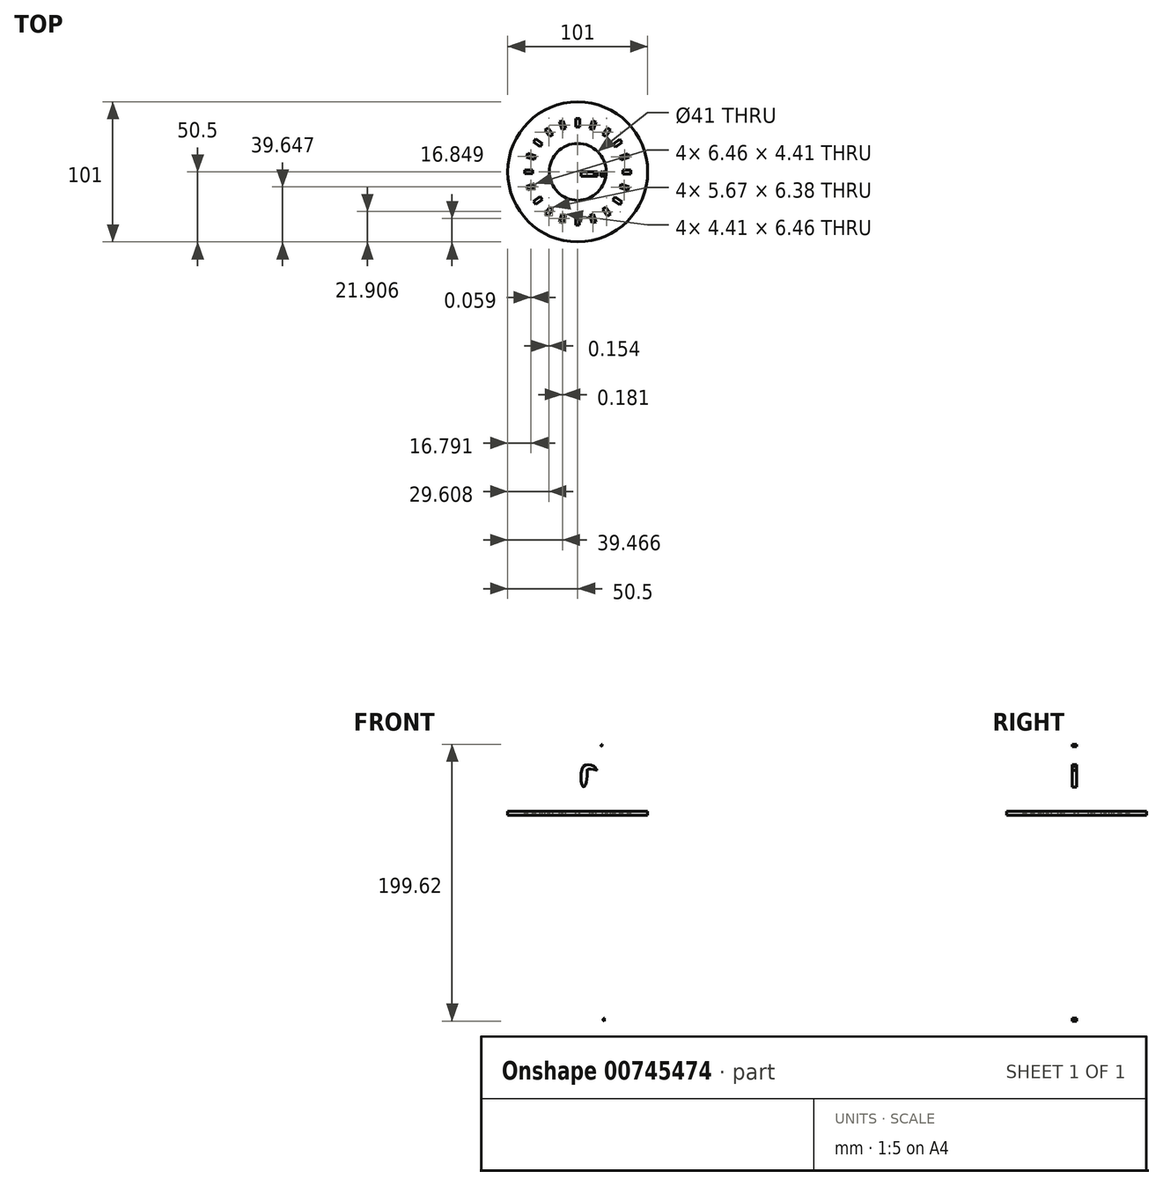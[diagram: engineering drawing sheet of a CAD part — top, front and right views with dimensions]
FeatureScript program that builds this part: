
annotation { "Feature Type Name" : "Feature", "Feature Type Description" : "" }
export const myFeature = defineFeature(function(context is Context, id is Id, definition is map)
    precondition{}
    {
        {
            var Q0;
            Q0=qCreatedBy(makeId("Front.planeOp"),FACE);
            var sketch = newSketch(context, id + "F0", { "sketchPlane" : qUnion([Q0])});
            skFitSpline(sketch, "E0", {"points": [v(18.94, 55.8) * mm, v(19.4, 42.74) * mm, v(74.56, -23) * mm, v(58.26, -54.69) * mm, v(18.93, -151.45) * mm], "startDerivative": vector(-29.4, -78.93) * mm, "endDerivative": vector(0, -157.02) * mm});
            skFitSpline(sketch, "E1.0", {"points": [v(9.57, 59.29) * mm, v(9.44, 58.92) * mm, v(9.1, 58.03) * mm, v(8.45, 56.18) * mm, v(7.84, 53.83) * mm, v(7.44, 51.02) * mm, v(7.45, 47.87) * mm, v(7.89, 45.1) * mm, v(8.5, 42.89) * mm, v(9.08, 41.22) * mm, v(9.67, 39.84) * mm, v(10.2, 38.74) * mm, v(10.64, 37.9) * mm, v(11.1, 37.1) * mm, v(11.72, 36.02) * mm, v(12.56, 34.7) * mm, v(13.65, 33.11) * mm, v(15.19, 31) * mm, v(17.29, 28.36) * mm, v(20.06, 25.1) * mm, v(23.05, 21.77) * mm, v(27.29, 17.22) * mm, v(32.95, 11.36) * mm, v(39.98, 4.2) * mm, v(46.9, -2.94) * mm, v(53.3, -9.85) * mm, v(57.89, -15.23) * mm, v(60.89, -19.14) * mm, v(62.74, -21.82) * mm, v(63.91, -23.77) * mm, v(64.6, -25.1) * mm, v(64.93, -25.82) * mm, v(65.13, -26.31) * mm, v(65.28, -26.74) * mm, v(65.42, -27.2) * mm, v(65.51, -27.62) * mm, v(65.56, -28.04) * mm, v(65.56, -28.36) * mm, v(65.5, -28.75) * mm, v(65.26, -29.42) * mm, v(64.73, -30.46) * mm, v(63.8, -31.88) * mm, v(62.48, -33.62) * mm, v(60.8, -35.67) * mm, v(58.8, -38.02) * mm, v(56.54, -40.67) * mm, v(54.08, -43.65) * mm, v(51.92, -46.42) * mm, v(50.14, -48.83) * mm, v(48.36, -51.35) * mm, v(46.15, -54.66) * mm, v(43.52, -58.88) * mm, v(40.9, -63.31) * mm, v(37.47, -69.48) * mm, v(33.27, -77.6) * mm, v(28.46, -87.76) * mm, v(23.96, -98.1) * mm, v(19.86, -108.39) * mm, v(16.26, -118.37) * mm, v(13.25, -127.84) * mm, v(11.3, -135.12) * mm, v(10.14, -140.51) * mm, v(9.48, -144.34) * mm, v(9.04, -147.97) * mm, v(8.93, -150.3) * mm, v(8.93, -151.45) * mm]});
            skLineSegment(sketch, "E2", {"start": v(18.94, 55.8) * mm, "end": v(8.37, 55.8) * mm});
            skLineSegment(sketch, "E3", {"start": v(18.93, -151.45) * mm, "end": v(8.93, -151.45) * mm});
            skLineSegment(sketch, "E4", {"start": v(14.05, 32.57) * mm, "end": v(16.18, 32.57) * mm});
            skFitSpline(sketch, "E5.trimOffspring", {"points": [v(9.57, 59.29) * mm, v(9.44, 58.92) * mm, v(9.1, 58.03) * mm, v(8.45, 56.18) * mm, v(7.84, 53.83) * mm, v(7.44, 51.02) * mm, v(7.45, 47.87) * mm, v(7.89, 45.1) * mm, v(8.5, 42.89) * mm, v(9.08, 41.22) * mm, v(9.67, 39.84) * mm, v(10.2, 38.74) * mm, v(10.64, 37.9) * mm, v(11.1, 37.1) * mm, v(11.72, 36.02) * mm, v(12.56, 34.7) * mm, v(13.65, 33.11) * mm, v(15.19, 31) * mm, v(17.29, 28.36) * mm, v(20.06, 25.1) * mm, v(23.05, 21.77) * mm, v(27.29, 17.22) * mm, v(32.95, 11.36) * mm, v(39.98, 4.2) * mm, v(46.9, -2.94) * mm, v(53.3, -9.85) * mm, v(57.89, -15.23) * mm, v(60.89, -19.14) * mm, v(62.74, -21.82) * mm, v(63.91, -23.77) * mm, v(64.6, -25.1) * mm, v(64.93, -25.82) * mm, v(65.13, -26.31) * mm, v(65.28, -26.74) * mm, v(65.42, -27.2) * mm, v(65.51, -27.62) * mm, v(65.56, -28.04) * mm, v(65.56, -28.36) * mm, v(65.5, -28.75) * mm, v(65.26, -29.42) * mm, v(64.73, -30.46) * mm, v(63.8, -31.88) * mm, v(62.48, -33.62) * mm, v(60.8, -35.67) * mm, v(58.8, -38.02) * mm, v(56.54, -40.67) * mm, v(54.08, -43.65) * mm, v(51.92, -46.42) * mm, v(50.14, -48.83) * mm, v(48.36, -51.35) * mm, v(46.15, -54.66) * mm, v(43.52, -58.88) * mm, v(40.9, -63.31) * mm, v(37.47, -69.48) * mm, v(33.27, -77.6) * mm, v(28.46, -87.76) * mm, v(23.96, -98.1) * mm, v(19.86, -108.39) * mm, v(16.26, -118.37) * mm, v(13.25, -127.84) * mm, v(11.3, -135.12) * mm, v(10.14, -140.51) * mm, v(9.48, -144.34) * mm, v(9.04, -147.97) * mm, v(8.93, -150.3) * mm, v(8.93, -151.45) * mm]});
            skFitSpline(sketch, "E6.trimOffspring", {"points": [v(9.57, 59.29) * mm, v(9.44, 58.92) * mm, v(9.1, 58.03) * mm, v(8.45, 56.18) * mm, v(7.84, 53.83) * mm, v(7.44, 51.02) * mm, v(7.45, 47.87) * mm, v(7.89, 45.1) * mm, v(8.5, 42.89) * mm, v(9.08, 41.22) * mm, v(9.67, 39.84) * mm, v(10.2, 38.74) * mm, v(10.64, 37.9) * mm, v(11.1, 37.1) * mm, v(11.72, 36.02) * mm, v(12.56, 34.7) * mm, v(13.65, 33.11) * mm, v(15.19, 31) * mm, v(17.29, 28.36) * mm, v(20.06, 25.1) * mm, v(23.05, 21.77) * mm, v(27.29, 17.22) * mm, v(32.95, 11.36) * mm, v(39.98, 4.2) * mm, v(46.9, -2.94) * mm, v(53.3, -9.85) * mm, v(57.89, -15.23) * mm, v(60.89, -19.14) * mm, v(62.74, -21.82) * mm, v(63.91, -23.77) * mm, v(64.6, -25.1) * mm, v(64.93, -25.82) * mm, v(65.13, -26.31) * mm, v(65.28, -26.74) * mm, v(65.42, -27.2) * mm, v(65.51, -27.62) * mm, v(65.56, -28.04) * mm, v(65.56, -28.36) * mm, v(65.5, -28.75) * mm, v(65.26, -29.42) * mm, v(64.73, -30.46) * mm, v(63.8, -31.88) * mm, v(62.48, -33.62) * mm, v(60.8, -35.67) * mm, v(58.8, -38.02) * mm, v(56.54, -40.67) * mm, v(54.08, -43.65) * mm, v(51.92, -46.42) * mm, v(50.14, -48.83) * mm, v(48.36, -51.35) * mm, v(46.15, -54.66) * mm, v(43.52, -58.88) * mm, v(40.9, -63.31) * mm, v(37.47, -69.48) * mm, v(33.27, -77.6) * mm, v(28.46, -87.76) * mm, v(23.96, -98.1) * mm, v(19.86, -108.39) * mm, v(16.26, -118.37) * mm, v(13.25, -127.84) * mm, v(11.3, -135.12) * mm, v(10.14, -140.51) * mm, v(9.48, -144.34) * mm, v(9.04, -147.97) * mm, v(8.93, -150.3) * mm, v(8.93, -151.45) * mm]});
            skLineSegment(sketch, "E7", {"start": v(42.73, 1.36) * mm, "end": v(42.73, 1.36) * mm});
            skPoint(sketch, "E8.orphan", {"position": v(0, -86.14) * mm});
            skPoint(sketch, "E9.end.orphan", {"position": v(15.52, -133.04) * mm});
            skFitSpline(sketch, "E10.trimOffspring", {"points": [v(9.57, 59.29) * mm, v(9.44, 58.92) * mm, v(9.1, 58.03) * mm, v(8.45, 56.18) * mm, v(7.84, 53.83) * mm, v(7.44, 51.02) * mm, v(7.45, 47.87) * mm, v(7.89, 45.1) * mm, v(8.5, 42.89) * mm, v(9.08, 41.22) * mm, v(9.67, 39.84) * mm, v(10.2, 38.74) * mm, v(10.64, 37.9) * mm, v(11.1, 37.1) * mm, v(11.72, 36.02) * mm, v(12.56, 34.7) * mm, v(13.65, 33.11) * mm, v(15.19, 31) * mm, v(17.29, 28.36) * mm, v(20.06, 25.1) * mm, v(23.05, 21.77) * mm, v(27.29, 17.22) * mm, v(32.95, 11.36) * mm, v(39.98, 4.2) * mm, v(46.9, -2.94) * mm, v(53.3, -9.85) * mm, v(57.89, -15.23) * mm, v(60.89, -19.14) * mm, v(62.74, -21.82) * mm, v(63.91, -23.77) * mm, v(64.6, -25.1) * mm, v(64.93, -25.82) * mm, v(65.13, -26.31) * mm, v(65.28, -26.74) * mm, v(65.42, -27.2) * mm, v(65.51, -27.62) * mm, v(65.56, -28.04) * mm, v(65.56, -28.36) * mm, v(65.5, -28.75) * mm, v(65.26, -29.42) * mm, v(64.73, -30.46) * mm, v(63.8, -31.88) * mm, v(62.48, -33.62) * mm, v(60.8, -35.67) * mm, v(58.8, -38.02) * mm, v(56.54, -40.67) * mm, v(54.08, -43.65) * mm, v(51.92, -46.42) * mm, v(50.14, -48.83) * mm, v(48.36, -51.35) * mm, v(46.15, -54.66) * mm, v(43.52, -58.88) * mm, v(40.9, -63.31) * mm, v(37.47, -69.48) * mm, v(33.27, -77.6) * mm, v(28.46, -87.76) * mm, v(23.96, -98.1) * mm, v(19.86, -108.39) * mm, v(16.26, -118.37) * mm, v(13.25, -127.84) * mm, v(11.3, -135.12) * mm, v(10.14, -140.51) * mm, v(9.48, -144.34) * mm, v(9.04, -147.97) * mm, v(8.93, -150.3) * mm, v(8.93, -151.45) * mm]});
            skLineSegment(sketch, "E11", {"start": v(14.05, 32.57) * mm, "end": v(21.01, 32.57) * mm});
            skLineSegment(sketch, "E12", {"start": v(21.01, 32.57) * mm, "end": v(21.01, 29.66) * mm});
            skLineSegment(sketch, "E13", {"start": v(21.01, 29.66) * mm, "end": v(16.36, 29.66) * mm});
            skLineSegment(sketch, "E14", {"start": v(59.17, -16.92) * mm, "end": v(59.17, -16.92) * mm});
            skFitSpline(sketch, "E15.trimOffspring", {"points": [v(9.57, 59.29) * mm, v(9.44, 58.92) * mm, v(9.1, 58.03) * mm, v(8.45, 56.18) * mm, v(7.84, 53.83) * mm, v(7.44, 51.02) * mm, v(7.45, 47.87) * mm, v(7.89, 45.1) * mm, v(8.5, 42.89) * mm, v(9.08, 41.22) * mm, v(9.67, 39.84) * mm, v(10.2, 38.74) * mm, v(10.64, 37.9) * mm, v(11.1, 37.1) * mm, v(11.72, 36.02) * mm, v(12.56, 34.7) * mm, v(13.65, 33.11) * mm, v(15.19, 31) * mm, v(17.29, 28.36) * mm, v(20.06, 25.1) * mm, v(23.05, 21.77) * mm, v(27.29, 17.22) * mm, v(32.95, 11.36) * mm, v(39.98, 4.2) * mm, v(46.9, -2.94) * mm, v(53.3, -9.85) * mm, v(57.89, -15.23) * mm, v(60.89, -19.14) * mm, v(62.74, -21.82) * mm, v(63.91, -23.77) * mm, v(64.6, -25.1) * mm, v(64.93, -25.82) * mm, v(65.13, -26.31) * mm, v(65.28, -26.74) * mm, v(65.42, -27.2) * mm, v(65.51, -27.62) * mm, v(65.56, -28.04) * mm, v(65.56, -28.36) * mm, v(65.5, -28.75) * mm, v(65.26, -29.42) * mm, v(64.73, -30.46) * mm, v(63.8, -31.88) * mm, v(62.48, -33.62) * mm, v(60.8, -35.67) * mm, v(58.8, -38.02) * mm, v(56.54, -40.67) * mm, v(54.08, -43.65) * mm, v(51.92, -46.42) * mm, v(50.14, -48.83) * mm, v(48.36, -51.35) * mm, v(46.15, -54.66) * mm, v(43.52, -58.88) * mm, v(40.9, -63.31) * mm, v(37.47, -69.48) * mm, v(33.27, -77.6) * mm, v(28.46, -87.76) * mm, v(23.96, -98.1) * mm, v(19.86, -108.39) * mm, v(16.26, -118.37) * mm, v(13.25, -127.84) * mm, v(11.3, -135.12) * mm, v(10.14, -140.51) * mm, v(9.48, -144.34) * mm, v(9.04, -147.97) * mm, v(8.93, -150.3) * mm, v(8.93, -151.45) * mm]});
            skLineSegment(sketch, "E16", {"start": v(15.52, -120.8) * mm, "end": v(18.75, -120.8) * mm});
            skLineSegment(sketch, "E17", {"start": v(18.75, -123.72) * mm, "end": v(14.58, -123.72) * mm});
            skLineSegment(sketch, "E18", {"start": v(58.14, -15.63) * mm, "end": v(58.14, -15.63) * mm});
            skPoint(sketch, "E19.end.orphan", {"position": v(28.86, -104.28) * mm});
            skPoint(sketch, "E19.start.orphan", {"position": v(28.86, -101.3) * mm});
            skFitSpline(sketch, "E20.trimOffspring", {"points": [v(9.57, 59.29) * mm, v(9.44, 58.92) * mm, v(9.1, 58.03) * mm, v(8.45, 56.18) * mm, v(7.84, 53.83) * mm, v(7.44, 51.02) * mm, v(7.45, 47.87) * mm, v(7.89, 45.1) * mm, v(8.5, 42.89) * mm, v(9.08, 41.22) * mm, v(9.67, 39.84) * mm, v(10.2, 38.74) * mm, v(10.64, 37.9) * mm, v(11.1, 37.1) * mm, v(11.72, 36.02) * mm, v(12.56, 34.7) * mm, v(13.65, 33.11) * mm, v(15.19, 31) * mm, v(17.29, 28.36) * mm, v(20.06, 25.1) * mm, v(23.05, 21.77) * mm, v(27.29, 17.22) * mm, v(32.95, 11.36) * mm, v(39.98, 4.2) * mm, v(46.9, -2.94) * mm, v(53.3, -9.85) * mm, v(57.89, -15.23) * mm, v(60.89, -19.14) * mm, v(62.74, -21.82) * mm, v(63.91, -23.77) * mm, v(64.6, -25.1) * mm, v(64.93, -25.82) * mm, v(65.13, -26.31) * mm, v(65.28, -26.74) * mm, v(65.42, -27.2) * mm, v(65.51, -27.62) * mm, v(65.56, -28.04) * mm, v(65.56, -28.36) * mm, v(65.5, -28.75) * mm, v(65.26, -29.42) * mm, v(64.73, -30.46) * mm, v(63.8, -31.88) * mm, v(62.48, -33.62) * mm, v(60.8, -35.67) * mm, v(58.8, -38.02) * mm, v(56.54, -40.67) * mm, v(54.08, -43.65) * mm, v(51.92, -46.42) * mm, v(50.14, -48.83) * mm, v(48.36, -51.35) * mm, v(46.15, -54.66) * mm, v(43.52, -58.88) * mm, v(40.9, -63.31) * mm, v(37.47, -69.48) * mm, v(33.27, -77.6) * mm, v(28.46, -87.76) * mm, v(23.96, -98.1) * mm, v(19.86, -108.39) * mm, v(16.26, -118.37) * mm, v(13.25, -127.84) * mm, v(11.3, -135.12) * mm, v(10.14, -140.51) * mm, v(9.48, -144.34) * mm, v(9.04, -147.97) * mm, v(8.93, -150.3) * mm, v(8.93, -151.45) * mm]});
            skLineSegment(sketch, "E21", {"start": v(18.75, -120.8) * mm, "end": v(20.6, -120.8) * mm});
            skLineSegment(sketch, "E22", {"start": v(20.6, -120.8) * mm, "end": v(20.6, -123.72) * mm});
            skLineSegment(sketch, "E23", {"start": v(20.6, -123.72) * mm, "end": v(18.75, -123.72) * mm});
            skLineSegment(sketch, "E24", {"start": v(17.74, 29.66) * mm, "end": v(16.27, 29.66) * mm});
            skFitSpline(sketch, "E25", {"points": [v(17.59, 51.26) * mm, v(16.83, 50.41) * mm, v(17.46, 49.64) * mm], "startDerivative": vector(-2.22, -1.65) * mm, "endDerivative": vector(2, -1.58) * mm});
            skFitSpline(sketch, "E26", {"points": [v(19.35, -146.2) * mm, v(18.22, -147.38) * mm, v(19.1, -148.36) * mm], "startDerivative": vector(-3.21, -2.27) * mm, "endDerivative": vector(2.83, -2.03) * mm});
            skFitSpline(sketch, "E27", {"points": [v(12.06, 35.49) * mm, v(4.24, 35.47) * mm, v(2.8, 22.72) * mm, v(4.33, 20.54) * mm, v(5.85, 22.5) * mm, v(6.9, 30.81) * mm, v(7.03, 33.16) * mm, v(14.05, 32.57) * mm], "startDerivative": vector(-54.48, 16.67) * mm, "endDerivative": vector(58.18, -11.46) * mm});
            skSolve(sketch);
        }
        {
            var Q0;
            Q0=qSketchRegion(id+"F0",true);
            extrude(context, id + "F1", {"entities" : qUnion([Q0]), "depth" : 3 * mm, "offsetDistance" : 25 * mm});
        }
        {
            var Q0;
            Q0=qCreatedBy(makeId("Top.planeOp"),FACE);
            var sketch = newSketch(context, id + "F2", { "sketchPlane" : qUnion([Q0])});
            skCircle(sketch, "E28", {"center": v(0, 0) * mm, "radius": 20.5 * mm});
            skCircle(sketch, "E29", {"center": v(0, 0) * mm, "radius": 50.5 * mm});
            skSolve(sketch);
        }
        {
            var Q0;
            Q0=qSketchRegion(id+"F2",true);
            extrude(context, id + "F3", {"entities" : qUnion([Q0]), "depth" : 3 * mm, "offsetDistance" : 25 * mm});
        }
        {
            var Q0;
            Q0=makeQuery(id+"F3.opExtrude","CAP_FACE",FACE,{"disambiguationData":[OSD([sQuery(id+"F2.wireOp",EDGE,"E28"),sQuery(id+"F2.wireOp",EDGE,"E29")])],"isStart":false});
            var sketch = newSketch(context, id + "F4", { "sketchPlane" : qUnion([Q0])});
            skLineSegment(sketch, "E30.bottom", {"start": v(-38.37, 1.45) * mm, "end": v(-32.46, 1.45) * mm});
            skLineSegment(sketch, "E30.top", {"start": v(-38.37, -1.26) * mm, "end": v(-32.46, -1.26) * mm});
            skLineSegment(sketch, "E30.left", {"start": v(-38.37, 1.45) * mm, "end": v(-38.37, -1.26) * mm});
            skLineSegment(sketch, "E30.right", {"start": v(-32.46, 1.45) * mm, "end": v(-32.46, -1.26) * mm});
            skLineSegment(sketch, "E31.1.0", {"start": v(-36.94, -10.48) * mm, "end": v(-31.32, -8.65) * mm});
            skLineSegment(sketch, "E31.1.1", {"start": v(-31.32, -8.65) * mm, "end": v(-30.48, -11.23) * mm});
            skLineSegment(sketch, "E31.1.2", {"start": v(-36.1, -13.06) * mm, "end": v(-30.48, -11.23) * mm});
            skLineSegment(sketch, "E31.1.3", {"start": v(-36.94, -10.48) * mm, "end": v(-36.1, -13.06) * mm});
            skLineSegment(sketch, "E31.2.0", {"start": v(-31.9, -21.38) * mm, "end": v(-27.11, -17.9) * mm});
            skLineSegment(sketch, "E31.2.1", {"start": v(-27.11, -17.9) * mm, "end": v(-25.52, -20.1) * mm});
            skLineSegment(sketch, "E31.2.2", {"start": v(-30.3, -23.57) * mm, "end": v(-25.52, -20.1) * mm});
            skLineSegment(sketch, "E31.2.3", {"start": v(-31.9, -21.38) * mm, "end": v(-30.3, -23.57) * mm});
            skLineSegment(sketch, "E31.3.0", {"start": v(-23.73, -30.19) * mm, "end": v(-20.25, -25.4) * mm});
            skLineSegment(sketch, "E31.3.1", {"start": v(-20.25, -25.4) * mm, "end": v(-18.06, -27) * mm});
            skLineSegment(sketch, "E31.3.2", {"start": v(-21.53, -31.78) * mm, "end": v(-18.06, -27) * mm});
            skLineSegment(sketch, "E31.3.3", {"start": v(-23.73, -30.19) * mm, "end": v(-21.53, -31.78) * mm});
            skLineSegment(sketch, "E31.4.0", {"start": v(-13.24, -36.04) * mm, "end": v(-11.41, -30.42) * mm});
            skLineSegment(sketch, "E31.4.1", {"start": v(-11.41, -30.42) * mm, "end": v(-8.83, -31.26) * mm});
            skLineSegment(sketch, "E31.4.2", {"start": v(-10.66, -36.88) * mm, "end": v(-8.83, -31.26) * mm});
            skLineSegment(sketch, "E31.4.3", {"start": v(-13.24, -36.04) * mm, "end": v(-10.66, -36.88) * mm});
            skLineSegment(sketch, "E31.5.0", {"start": v(-1.45, -38.37) * mm, "end": v(-1.45, -32.46) * mm});
            skLineSegment(sketch, "E31.5.1", {"start": v(-1.45, -32.46) * mm, "end": v(1.26, -32.46) * mm});
            skLineSegment(sketch, "E31.5.2", {"start": v(1.26, -38.37) * mm, "end": v(1.26, -32.46) * mm});
            skLineSegment(sketch, "E31.5.3", {"start": v(-1.45, -38.37) * mm, "end": v(1.26, -38.37) * mm});
            skLineSegment(sketch, "E31.6.0", {"start": v(10.48, -36.94) * mm, "end": v(8.65, -31.32) * mm});
            skLineSegment(sketch, "E31.6.1", {"start": v(8.65, -31.32) * mm, "end": v(11.23, -30.48) * mm});
            skLineSegment(sketch, "E31.6.2", {"start": v(13.06, -36.1) * mm, "end": v(11.23, -30.48) * mm});
            skLineSegment(sketch, "E31.6.3", {"start": v(10.48, -36.94) * mm, "end": v(13.06, -36.1) * mm});
            skLineSegment(sketch, "E31.7.0", {"start": v(21.38, -31.9) * mm, "end": v(17.9, -27.11) * mm});
            skLineSegment(sketch, "E31.7.1", {"start": v(17.9, -27.11) * mm, "end": v(20.1, -25.52) * mm});
            skLineSegment(sketch, "E31.7.2", {"start": v(23.57, -30.3) * mm, "end": v(20.1, -25.52) * mm});
            skLineSegment(sketch, "E31.7.3", {"start": v(21.38, -31.9) * mm, "end": v(23.57, -30.3) * mm});
            skLineSegment(sketch, "E31.8.0", {"start": v(30.19, -23.73) * mm, "end": v(25.4, -20.25) * mm});
            skLineSegment(sketch, "E31.8.1", {"start": v(25.4, -20.25) * mm, "end": v(27, -18.06) * mm});
            skLineSegment(sketch, "E31.8.2", {"start": v(31.78, -21.53) * mm, "end": v(27, -18.06) * mm});
            skLineSegment(sketch, "E31.8.3", {"start": v(30.19, -23.73) * mm, "end": v(31.78, -21.53) * mm});
            skLineSegment(sketch, "E31.9.0", {"start": v(36.04, -13.24) * mm, "end": v(30.42, -11.41) * mm});
            skLineSegment(sketch, "E31.9.1", {"start": v(30.42, -11.41) * mm, "end": v(31.26, -8.83) * mm});
            skLineSegment(sketch, "E31.9.2", {"start": v(36.88, -10.66) * mm, "end": v(31.26, -8.83) * mm});
            skLineSegment(sketch, "E31.9.3", {"start": v(36.04, -13.24) * mm, "end": v(36.88, -10.66) * mm});
            skLineSegment(sketch, "E31.10.0", {"start": v(38.37, -1.45) * mm, "end": v(32.46, -1.45) * mm});
            skLineSegment(sketch, "E31.10.1", {"start": v(32.46, -1.45) * mm, "end": v(32.46, 1.26) * mm});
            skLineSegment(sketch, "E31.10.2", {"start": v(38.37, 1.26) * mm, "end": v(32.46, 1.26) * mm});
            skLineSegment(sketch, "E31.10.3", {"start": v(38.37, -1.45) * mm, "end": v(38.37, 1.26) * mm});
            skLineSegment(sketch, "E31.11.0", {"start": v(36.94, 10.48) * mm, "end": v(31.32, 8.65) * mm});
            skLineSegment(sketch, "E31.11.1", {"start": v(31.32, 8.65) * mm, "end": v(30.48, 11.23) * mm});
            skLineSegment(sketch, "E31.11.2", {"start": v(36.1, 13.06) * mm, "end": v(30.48, 11.23) * mm});
            skLineSegment(sketch, "E31.11.3", {"start": v(36.94, 10.48) * mm, "end": v(36.1, 13.06) * mm});
            skLineSegment(sketch, "E31.12.0", {"start": v(31.9, 21.38) * mm, "end": v(27.11, 17.9) * mm});
            skLineSegment(sketch, "E31.12.1", {"start": v(27.11, 17.9) * mm, "end": v(25.52, 20.1) * mm});
            skLineSegment(sketch, "E31.12.2", {"start": v(30.3, 23.57) * mm, "end": v(25.52, 20.1) * mm});
            skLineSegment(sketch, "E31.12.3", {"start": v(31.9, 21.38) * mm, "end": v(30.3, 23.57) * mm});
            skLineSegment(sketch, "E31.13.0", {"start": v(23.73, 30.19) * mm, "end": v(20.25, 25.4) * mm});
            skLineSegment(sketch, "E31.13.1", {"start": v(20.25, 25.4) * mm, "end": v(18.06, 27) * mm});
            skLineSegment(sketch, "E31.13.2", {"start": v(21.53, 31.78) * mm, "end": v(18.06, 27) * mm});
            skLineSegment(sketch, "E31.13.3", {"start": v(23.73, 30.19) * mm, "end": v(21.53, 31.78) * mm});
            skLineSegment(sketch, "E31.14.0", {"start": v(13.24, 36.04) * mm, "end": v(11.41, 30.42) * mm});
            skLineSegment(sketch, "E31.14.1", {"start": v(11.41, 30.42) * mm, "end": v(8.83, 31.26) * mm});
            skLineSegment(sketch, "E31.14.2", {"start": v(10.66, 36.88) * mm, "end": v(8.83, 31.26) * mm});
            skLineSegment(sketch, "E31.14.3", {"start": v(13.24, 36.04) * mm, "end": v(10.66, 36.88) * mm});
            skLineSegment(sketch, "E31.15.0", {"start": v(1.45, 38.37) * mm, "end": v(1.45, 32.46) * mm});
            skLineSegment(sketch, "E31.15.1", {"start": v(1.45, 32.46) * mm, "end": v(-1.26, 32.46) * mm});
            skLineSegment(sketch, "E31.15.2", {"start": v(-1.26, 38.37) * mm, "end": v(-1.26, 32.46) * mm});
            skLineSegment(sketch, "E31.15.3", {"start": v(1.45, 38.37) * mm, "end": v(-1.26, 38.37) * mm});
            skLineSegment(sketch, "E31.16.0", {"start": v(-10.48, 36.94) * mm, "end": v(-8.65, 31.32) * mm});
            skLineSegment(sketch, "E31.16.1", {"start": v(-8.65, 31.32) * mm, "end": v(-11.23, 30.48) * mm});
            skLineSegment(sketch, "E31.16.2", {"start": v(-13.06, 36.1) * mm, "end": v(-11.23, 30.48) * mm});
            skLineSegment(sketch, "E31.16.3", {"start": v(-10.48, 36.94) * mm, "end": v(-13.06, 36.1) * mm});
            skLineSegment(sketch, "E31.17.0", {"start": v(-21.38, 31.9) * mm, "end": v(-17.9, 27.11) * mm});
            skLineSegment(sketch, "E31.17.1", {"start": v(-17.9, 27.11) * mm, "end": v(-20.1, 25.52) * mm});
            skLineSegment(sketch, "E31.17.2", {"start": v(-23.57, 30.3) * mm, "end": v(-20.1, 25.52) * mm});
            skLineSegment(sketch, "E31.17.3", {"start": v(-21.38, 31.9) * mm, "end": v(-23.57, 30.3) * mm});
            skLineSegment(sketch, "E31.18.0", {"start": v(-30.19, 23.73) * mm, "end": v(-25.4, 20.25) * mm});
            skLineSegment(sketch, "E31.18.1", {"start": v(-25.4, 20.25) * mm, "end": v(-27, 18.06) * mm});
            skLineSegment(sketch, "E31.18.2", {"start": v(-31.78, 21.53) * mm, "end": v(-27, 18.06) * mm});
            skLineSegment(sketch, "E31.18.3", {"start": v(-30.19, 23.73) * mm, "end": v(-31.78, 21.53) * mm});
            skLineSegment(sketch, "E31.19.0", {"start": v(-36.04, 13.24) * mm, "end": v(-30.42, 11.41) * mm});
            skLineSegment(sketch, "E31.19.1", {"start": v(-30.42, 11.41) * mm, "end": v(-31.26, 8.83) * mm});
            skLineSegment(sketch, "E31.19.2", {"start": v(-36.88, 10.66) * mm, "end": v(-31.26, 8.83) * mm});
            skLineSegment(sketch, "E31.19.3", {"start": v(-36.04, 13.24) * mm, "end": v(-36.88, 10.66) * mm});
            skPoint(sketch, "E31.center", {"position": v(0, 0) * mm});
            skSolve(sketch);
        }
        {
            var Q0;
            Q0 = qSketchRegion(id + "F4", true);
            extrude(context, id + "F5", {"entities" : qUnion([Q0]), "operationType" : NewBodyOperationType.REMOVE, "oppositeDirection" : true, "depth" : 25 * mm, "offsetDistance" : 25 * mm});
        }
    });
